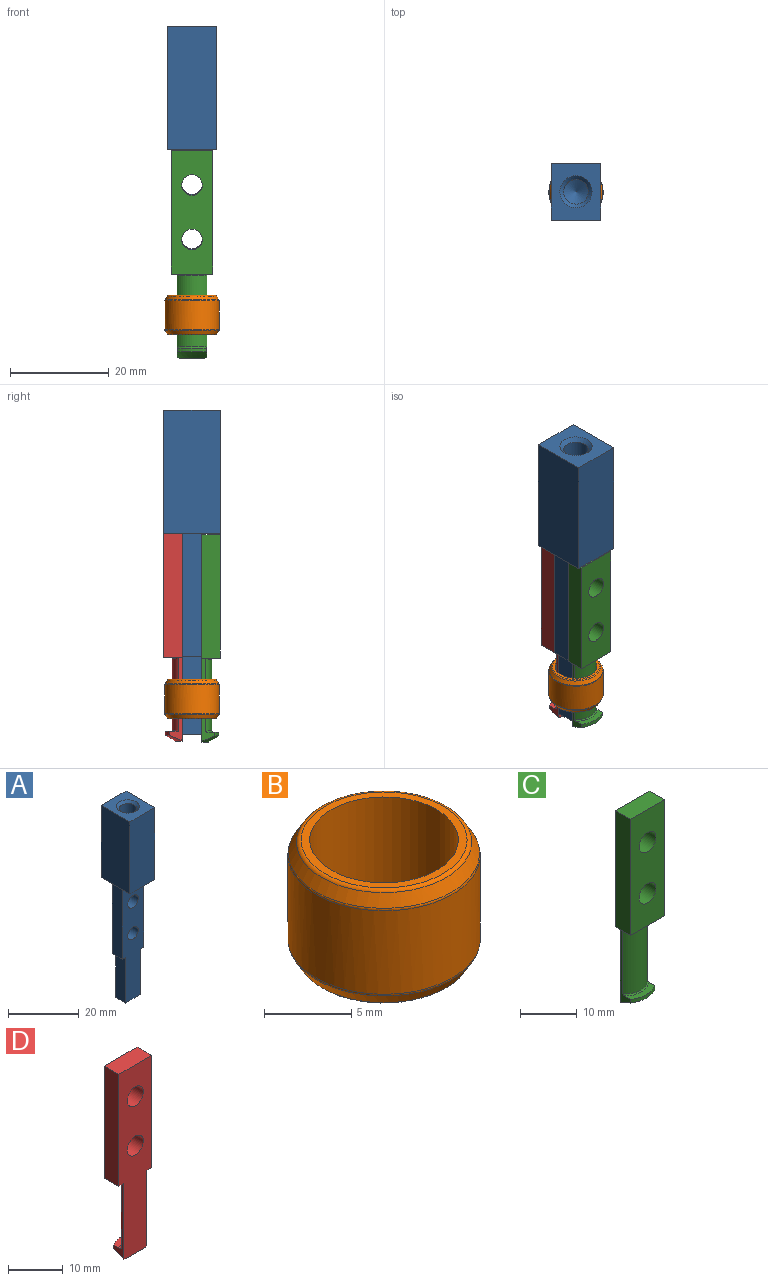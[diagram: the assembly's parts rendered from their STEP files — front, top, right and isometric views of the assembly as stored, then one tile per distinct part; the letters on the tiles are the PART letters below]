
ASSEMBLY  parts=4 mates=3
PART A: 20 faces, bbox 10x11.5x65.8 mm
  f0: plane 4x1.25mm, normal (0,0,-1), area 5mm2, adj f7,f9,f10,f13
  f1: plane 25x10mm, normal (0,1,0), area 250mm2, adj f2,f4,f5,f6
  f2: plane 25x11.5mm, normal (-1,0,0), area 287.5mm2, adj f1,f3,f5,f6
  f3: plane 25x10mm, normal (0,-1,0), area 250mm2, adj f2,f4,f5,f6
  f4: plane 25x11.5mm, normal (1,0,0), area 287.5mm2, adj f1,f3,f5,f6
  f5: plane 11.5x10mm, normal (0,0,1), area 81.8mm2, adj f1,f2,f3,f4,f19
  f6: plane 11.5x10mm, normal (0,0,-1), area 81mm2, adj f1,f2,f3,f4,f7,f8,f9,f10
  f7: plane 40.75x8.5mm, normal (0,-1,0), area 279.3mm2, adj f0,f6,f8,f10,f11,f12,f13,f14
  f8: plane 25x4mm, normal (-1,0,0), area 100mm2, adj f6,f7,f9,f11
  f9: plane 40.75x8.5mm, normal (0,1,0), area 279.3mm2, adj f0,f6,f8,f10,f11,f12,f13,f14
  f10: plane 25x4mm, normal (1,0,0), area 100mm2, adj f0,f6,f7,f9
  f11: plane 4x1.25mm, normal (0,0,-1), area 5mm2, adj f7,f8,f9,f12
  f12: plane 15.75x4mm, normal (-1,0,0), area 63mm2, adj f7,f9,f11,f14
  f13: plane 15.75x4mm, normal (1,0,0), area 63mm2, adj f0,f7,f9,f14
  f14: plane 6x4mm, normal (0,0,-1), area 24mm2, adj f7,f9,f12,f13
  f15: cylinder r=2.1mm len=4.2mm, axis (0,-1,0), area 52.8mm2, adj f7,f9
  f16: cylinder r=2.1mm len=4.2mm, axis (0,-1,0), area 52.8mm2, adj f7,f9
  f17: cone r=0mm half-angle=59deg, axis (0,0,1), area 22.9mm2, adj f18
  f18: cylinder r=2.5mm len=19.25mm, axis (0,0,1), area 302.4mm2, adj f17,f19
  f19: cone r=2.5mm half-angle=45deg, axis (0,0,1), area 19.2mm2, adj f5,f18
PART B: 10 faces, bbox 11.9x11.9x8 mm
  f0: cylinder r=4.25mm len=8.5mm, axis (0,0,1), area 213.6mm2, adj f2,f3
  f1: cylinder r=5.5mm len=11mm, axis (0,0,1), area 201.8mm2, adj f6,f9
  f2: plane 9.5x9.5mm, normal (0,0,-1), area 14.1mm2, adj f0,f7
  f3: plane 9.5x9.5mm, normal (0,0,1), area 14.1mm2, adj f0,f8
  f4: cone r=5.5mm half-angle=30deg, axis (0,0,-1), area 29.6mm2, adj f8,f9
  f5: cone r=4.92mm half-angle=30deg, axis (0,0,1), area 29.6mm2, adj f6,f7
  f6: torus R=5.2mm, axis (0,0,-1), area 5.4mm2, adj f1,f5
  f7: torus R=4.75mm, axis (0,0,-1), area 9.7mm2, adj f2,f5
  f8: torus R=4.75mm, axis (0,0,-1), area 9.7mm2, adj f3,f4
  f9: torus R=5.2mm, axis (0,0,1), area 5.4mm2, adj f1,f4
PART C: 17 faces, bbox 9.2x4x42.1 mm
  f0: plane 6x2.44mm, normal (0,0,1), area 7.8mm2, adj f1,f4,f7,f16
  f1: cylinder r=5.45mm len=6mm, axis (0,0,1), area 4.8mm2, adj f0,f3,f4,f7
  f2: plane 5.21x1.29mm, normal (0,0,-1), area 4.7mm2, adj f3,f6
  f3: cone r=3.28mm half-angle=60deg, axis (0,0,1), area 16.5mm2, adj f1,f2,f4,f6,f7
  f4: plane 16.9x2.64mm, normal (1,0,0), area 13.1mm2, adj f0,f1,f3,f5,f6,f12,f15,f16
  f5: cylinder r=4mm len=14.5mm, axis (0,0,1), area 98.4mm2, adj f4,f7,f15,f16
  f6: plane 42.01x8.51mm, normal (0,1,0), area 286.7mm2, adj f2,f3,f4,f7,f8,f9,f11,f12
  f7: plane 16.9x2.64mm, normal (-1,0,0), area 13.1mm2, adj f0,f1,f3,f5,f6,f12,f15,f16
  f8: cylinder r=2.1mm len=4.2mm, axis (0,-1,0), area 49.5mm2, adj f6,f10
  f9: cylinder r=2.1mm len=4.2mm, axis (0,-1,0), area 49.5mm2, adj f6,f10
  f10: plane 25x8.5mm, normal (0,-1,0), area 184.8mm2, adj f8,f9,f11,f12,f13,f14
  f11: plane 8.5x3.75mm, normal (0,0,1), area 31.9mm2, adj f6,f10,f13,f14
  f12: plane 8.5x3.75mm, normal (0,0,-1), area 20.7mm2, adj f4,f6,f7,f10,f13,f14,f15
  f13: plane 25x3.75mm, normal (-1,0,0), area 93.8mm2, adj f6,f10,f11,f12
  f14: plane 25x3.75mm, normal (1,0,0), area 93.8mm2, adj f6,f10,f11,f12
  f15: torus R=4.25mm, axis (0,0,1), area 2.6mm2, adj f4,f5,f7,f12
  f16: torus R=4.25mm, axis (0,0,-1), area 2.6mm2, adj f0,f4,f5,f7
PART D: 17 faces, bbox 9.2x4x42.1 mm
  f0: plane 8.5x3.75mm, normal (0,0,-1), area 20.7mm2, adj f1,f10,f11,f12,f13,f14,f15
  f1: plane 25x8.5mm, normal (0,1,0), area 184.8mm2, adj f0,f2,f3,f9,f13,f14
  f2: cylinder r=2.1mm len=4.2mm, axis (0,-1,0), area 49.5mm2, adj f1,f12
  f3: cylinder r=2.1mm len=4.2mm, axis (0,-1,0), area 49.5mm2, adj f1,f12
  f4: cylinder r=4mm len=14.5mm, axis (0,0,1), area 98.4mm2, adj f10,f11,f15,f16
  f5: cylinder r=5.45mm len=6mm, axis (0,0,1), area 4.8mm2, adj f7,f8,f10,f11
  f6: plane 5.21x1.29mm, normal (0,0,-1), area 4.7mm2, adj f8,f12
  f7: plane 6x2.44mm, normal (0,0,1), area 7.8mm2, adj f5,f10,f11,f16
  f8: cone r=3.28mm half-angle=60deg, axis (0,0,1), area 16.5mm2, adj f5,f6,f10,f11,f12
  f9: plane 8.5x3.75mm, normal (0,0,1), area 31.9mm2, adj f1,f12,f13,f14
  f10: plane 16.9x2.64mm, normal (-1,0,0), area 13.1mm2, adj f0,f4,f5,f7,f8,f12,f15,f16
  f11: plane 16.9x2.64mm, normal (1,0,0), area 13.1mm2, adj f0,f4,f5,f7,f8,f12,f15,f16
  f12: plane 42.01x8.51mm, normal (0,-1,0), area 286.7mm2, adj f0,f2,f3,f6,f8,f9,f10,f11
  f13: plane 25x3.75mm, normal (-1,0,0), area 93.8mm2, adj f0,f1,f9,f12
  f14: plane 25x3.75mm, normal (1,0,0), area 93.8mm2, adj f0,f1,f9,f12
  f15: torus R=4.25mm, axis (0,0,1), area 2.6mm2, adj f0,f4,f10,f11
  f16: torus R=4.25mm, axis (0,0,-1), area 2.6mm2, adj f4,f7,f10,f11
PLACE A t=(8.97,42.99,-10.23)mm
PLACE B t=(8.97,42.99,-9.76)mm
PLACE C t=(8.97,42.99,-10.44)mm
PLACE D t=(8.97,42.99,-10.3)mm
MATE parallel C.f11 <-> A.f6  axis (0,0,-1) through (13.22,40.99,14.56)mm
MATE parallel B.f0 <-> D.f4  axis (0,0,1) through (8.97,42.99,-18.76)mm
MATE parallel D.f9 <-> A.f6  axis (0,0,-1) through (13.22,44.99,14.7)mm
